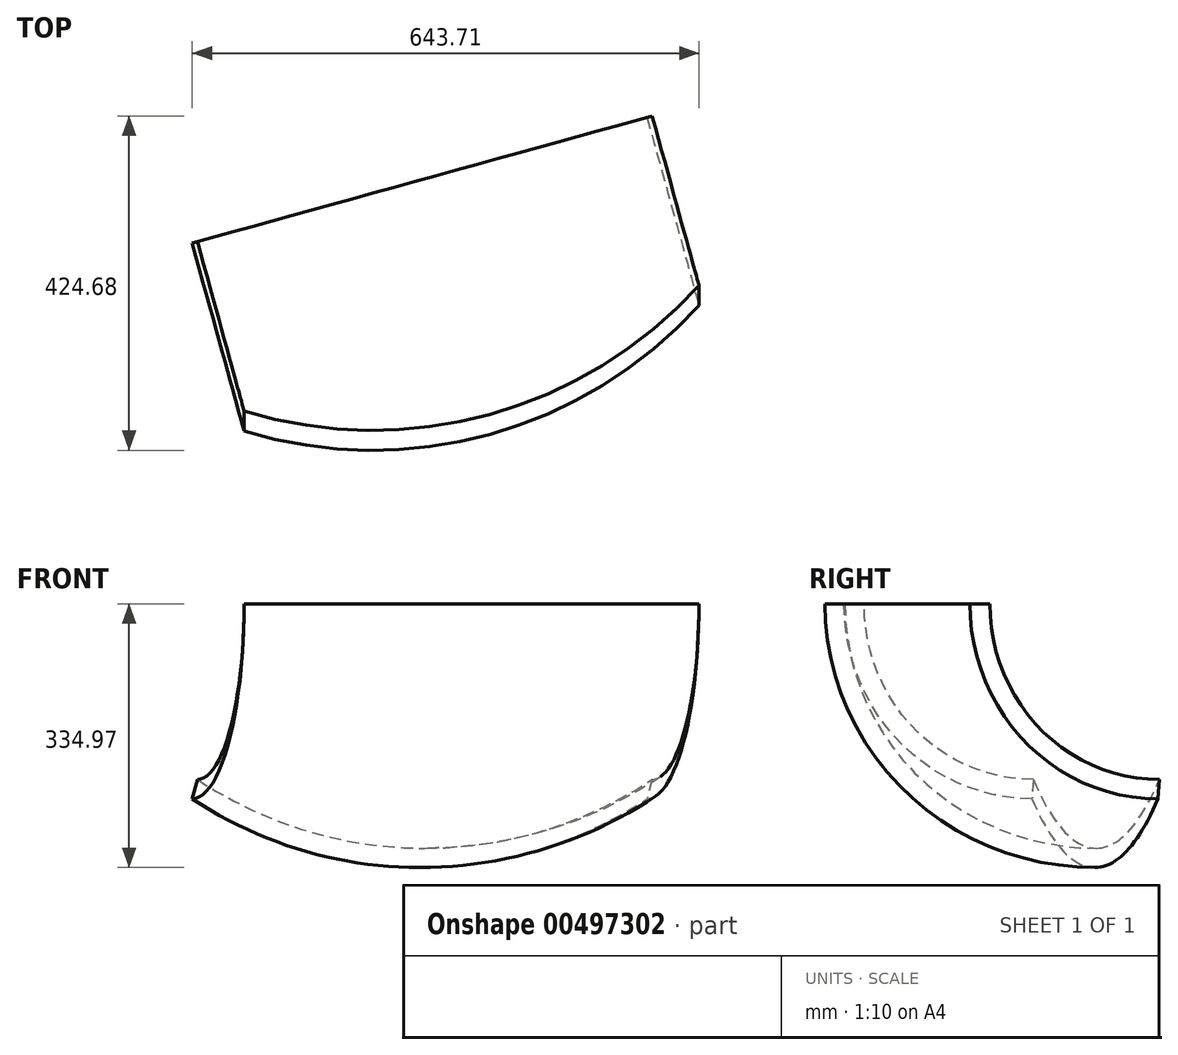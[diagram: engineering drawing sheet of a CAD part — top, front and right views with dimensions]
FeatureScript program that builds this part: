
annotation { "Feature Type Name" : "Feature", "Feature Type Description" : "" }
export const myFeature = defineFeature(function(context is Context, id is Id, definition is map)
    precondition{}
    {
        {
            var Q0;
            Q0=qCreatedBy(makeId("Top.planeOp"),FACE);
            var sketch = newSketch(context, id + "F0", { "sketchPlane" : qUnion([Q0])});
            skArc(sketch, "E0.MirrorCS", {"start": v(-333.28, -52.47) * mm, "mid": v(-21.17, -56.75) * mm, "end": v(244.44, 107.21) * mm});
            skArc(sketch, "E1.MirrorCS", {"start": v(-333.28, -27.07) * mm, "mid": v(-21.17, -31.35) * mm, "end": v(244.44, 132.61) * mm});
            skLineSegment(sketch, "E2", {"start": v(-333.28, -27.07) * mm, "end": v(-333.28, -52.47) * mm});
            skLineSegment(sketch, "E3", {"start": v(244.44, 132.61) * mm, "end": v(244.44, 107.21) * mm});
            skLineSegment(sketch, "E4", {"start": v(-251.58, 227.1) * mm, "end": v(37.28, 306.94) * mm});
            skSolve(sketch);
        }
        {
            var Q0;
            Q0=makeQuery(id+"F0.imprint","IMPRINT",FACE,{"disambiguationData":[TD([[makeQuery(id+"F0.imprint","IMPRINT",EDGE,{"derivedFrom":sQuery(id+"F0.wireOp",EDGE,"E0.MirrorCS")}),1.0]])]});
            var Q1;
            Q1=sQuery(id+"F0.wireOp",EDGE,"E4");
            revolve(context, id + "F1", {"entities" : qUnion([Q0]), "axis" : qUnion([Q1]), "revolveType" : RevolveType.ONE_DIRECTION, "angle" : 90 * degree});
        }
    });
